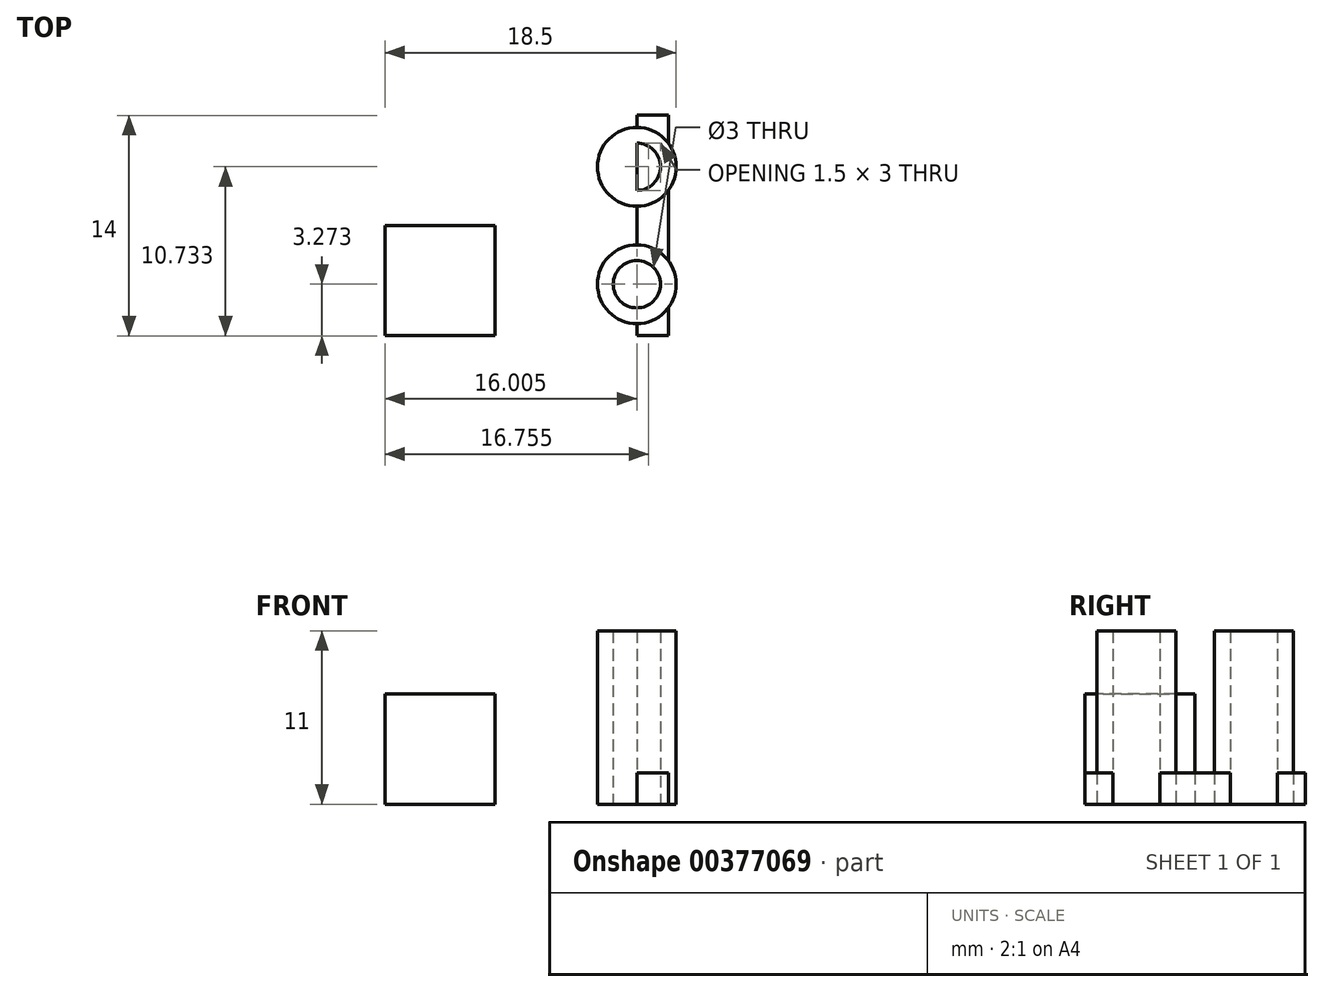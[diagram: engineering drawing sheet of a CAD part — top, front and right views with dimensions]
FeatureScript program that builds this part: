
annotation { "Feature Type Name" : "Feature", "Feature Type Description" : "" }
export const myFeature = defineFeature(function(context is Context, id is Id, definition is map)
    precondition{}
    {
        {
            var Q0;
            Q0=qCreatedBy(makeId("Top.planeOp"),FACE);
            var sketch = newSketch(context, id + "F0", { "sketchPlane" : qUnion([Q0])});
            skLineSegment(sketch, "E0.bottom", {"start": v(5.98, -1.35) * mm, "end": v(36.98, -1.35) * mm});
            skLineSegment(sketch, "E0.top", {"start": v(5.98, -15.35) * mm, "end": v(36.98, -15.35) * mm});
            skLineSegment(sketch, "E0.left", {"start": v(5.98, -1.35) * mm, "end": v(5.98, -15.35) * mm});
            skLineSegment(sketch, "E0.right", {"start": v(36.98, -1.35) * mm, "end": v(36.98, -15.35) * mm});
            skLineSegment(sketch, "E1", {"start": v(34.98, -1.35) * mm, "end": v(34.98, -15.35) * mm});
            skLineSegment(sketch, "E2", {"start": v(18.98, -15.35) * mm, "end": v(18.98, -8.35) * mm});
            skLineSegment(sketch, "E3", {"start": v(18.98, -8.35) * mm, "end": v(25.98, -8.35) * mm});
            skLineSegment(sketch, "E4", {"start": v(25.98, -8.35) * mm, "end": v(25.98, -15.35) * mm});
            skLineSegment(sketch, "E5", {"start": v(34.98, -1.35) * mm, "end": v(34.98, -3.35) * mm});
            skLineSegment(sketch, "E6", {"start": v(34.98, -3.35) * mm, "end": v(34.98, -5.89) * mm});
            skLineSegment(sketch, "E7", {"start": v(34.98, -15.35) * mm, "end": v(34.98, -13.35) * mm});
            skLineSegment(sketch, "E8", {"start": v(34.98, -13.35) * mm, "end": v(34.98, -10.8) * mm});
            skCircle(sketch, "E9", {"center": v(34.98, -12.08) * mm, "radius": 1.5 * mm});
            skCircle(sketch, "E10", {"center": v(34.98, -4.62) * mm, "radius": 1.5 * mm});
            skCircle(sketch, "E11", {"center": v(34.98, -4.62) * mm, "radius": 2.5 * mm});
            skCircle(sketch, "E12", {"center": v(34.98, -12.08) * mm, "radius": 2.5 * mm});
            skSolve(sketch);
        }
        {
            var Q0;
            {var subQ0=sQuery(id+"F0.wireOp",EDGE,"E2");Q0=makeQuery(id+"F0.imprint","IMPRINT",FACE,{"disambiguationData":[TD([[makeQuery(id+"F0.imprint","IMPRINT",EDGE,{"derivedFrom":subQ0}),-1.0]])]});}
            extrude(context, id + "F1", {"entities" : qUnion([Q0]), "depth" : 7 * mm});
        }
        {
            var Q0;
            {var subQ0=sQuery(id+"F0.wireOp",EDGE,"E10");var subQ1=sQuery(id+"F0.wireOp",EDGE,"E1");var subQ2=makeQuery(id+"F0.imprint","INTERSECT",VERTEX,{"derivedFrom":[subQ1,subQ0]});Q0=makeQuery(id+"F0.imprint","IMPRINT",FACE,{"disambiguationData":[TD([[makeQuery(id+"F0.imprint","IMPRINT",EDGE,{"disambiguationData":[TD([[subQ2,-1.0]])],"derivedFrom":subQ1}),-1.0]])]});}
            var Q1;
            {var subQ0=sQuery(id+"F0.wireOp",EDGE,"E6");Q1=makeQuery(id+"F0.imprint","IMPRINT",FACE,{"disambiguationData":[TD([[makeQuery(id+"F0.imprint","IMPRINT",EDGE,{"derivedFrom":subQ0}),-1.0]])]});}
            var Q2;
            {var subQ0=sQuery(id+"F0.wireOp",EDGE,"E6");Q2=makeQuery(id+"F0.imprint","IMPRINT",FACE,{"disambiguationData":[TD([[makeQuery(id+"F0.imprint","IMPRINT",EDGE,{"derivedFrom":subQ0}),1.0]])]});}
            var Q3;
            {var subQ5=sQuery(id+"F0.wireOp",EDGE,"E11");var subQ7=sQuery(id+"F0.wireOp",EDGE,"E0.right");var subQ8=makeQuery(id+"F0.imprint","INTERSECT",VERTEX,{"disambiguationData":[OD(0.0)],"derivedFrom":[subQ7,subQ5]});Q3=makeQuery(id+"F0.imprint","IMPRINT",FACE,{"disambiguationData":[TD([[makeQuery(id+"F0.imprint","IMPRINT",EDGE,{"disambiguationData":[TD([[subQ8,-1.0]])],"derivedFrom":subQ7}),-1.0]])]});}
            var Q4;
            {var subQ0=sQuery(id+"F0.wireOp",EDGE,"E11");var subQ1=sQuery(id+"F0.wireOp",EDGE,"E0.right");var subQ2=makeQuery(id+"F0.imprint","INTERSECT",VERTEX,{"disambiguationData":[OD(0.0)],"derivedFrom":[subQ1,subQ0]});Q4=makeQuery(id+"F0.imprint","IMPRINT",FACE,{"disambiguationData":[TD([[makeQuery(id+"F0.imprint","IMPRINT",EDGE,{"disambiguationData":[TD([[subQ2,-1.0]])],"derivedFrom":subQ1}),1.0]])]});}
            var Q5;
            {var subQ0=sQuery(id+"F0.wireOp",EDGE,"E8");Q5=makeQuery(id+"F0.imprint","IMPRINT",FACE,{"disambiguationData":[TD([[makeQuery(id+"F0.imprint","IMPRINT",EDGE,{"derivedFrom":subQ0}),-1.0]])]});}
            var Q6;
            {var subQ0=sQuery(id+"F0.wireOp",EDGE,"E12");var subQ1=sQuery(id+"F0.wireOp",EDGE,"E0.right");var subQ2=makeQuery(id+"F0.imprint","INTERSECT",VERTEX,{"disambiguationData":[OD(0.0)],"derivedFrom":[subQ1,subQ0]});Q6=makeQuery(id+"F0.imprint","IMPRINT",FACE,{"disambiguationData":[TD([[makeQuery(id+"F0.imprint","IMPRINT",EDGE,{"disambiguationData":[TD([[subQ2,-1.0]])],"derivedFrom":subQ1}),1.0]])]});}
            var Q7;
            {var subQ5=sQuery(id+"F0.wireOp",EDGE,"E12");var subQ7=sQuery(id+"F0.wireOp",EDGE,"E0.right");var subQ8=makeQuery(id+"F0.imprint","INTERSECT",VERTEX,{"disambiguationData":[OD(0.0)],"derivedFrom":[subQ7,subQ5]});Q7=makeQuery(id+"F0.imprint","IMPRINT",FACE,{"disambiguationData":[TD([[makeQuery(id+"F0.imprint","IMPRINT",EDGE,{"disambiguationData":[TD([[subQ8,-1.0]])],"derivedFrom":subQ7}),-1.0]])]});}
            var Q8;
            {var subQ0=sQuery(id+"F0.wireOp",EDGE,"E8");Q8=makeQuery(id+"F0.imprint","IMPRINT",FACE,{"disambiguationData":[TD([[makeQuery(id+"F0.imprint","IMPRINT",EDGE,{"derivedFrom":subQ0}),1.0]])]});}
            var Q9;
            {var subQ0=sQuery(id+"F0.wireOp",EDGE,"E12");var subQ1=sQuery(id+"F0.wireOp",EDGE,"E1");var subQ2=makeQuery(id+"F0.imprint","INTERSECT",VERTEX,{"derivedFrom":[subQ1,subQ0]});Q9=makeQuery(id+"F0.imprint","IMPRINT",FACE,{"disambiguationData":[TD([[makeQuery(id+"F0.imprint","IMPRINT",EDGE,{"disambiguationData":[TD([[subQ2,-1.0]])],"derivedFrom":subQ1}),-1.0]])]});}
            extrude(context, id + "F2", {"entities" : qUnion([Q0, Q1, Q2, Q3, Q4, Q5, Q6, Q7, Q8, Q9]), "depth" : 11 * mm});
        }
        {
            var Q0;
            {var subQ12=sQuery(id+"F0.wireOp",EDGE,"E0.left");Q0=makeQuery(id+"F0.imprint","IMPRINT",FACE,{"disambiguationData":[TD([[makeQuery(id+"F0.imprint","IMPRINT",EDGE,{"derivedFrom":subQ12}),1.0]])]});}
            var Q1;
            {var subQ0=sQuery(id+"F0.wireOp",EDGE,"E0.right");var subQ1=sQuery(id+"F0.wireOp",EDGE,"E0.top");var subQ2=makeQuery(id+"F0.imprint","INTERSECT",VERTEX,{"derivedFrom":[subQ1,subQ0]});Q1=makeQuery(id+"F0.imprint","IMPRINT",FACE,{"disambiguationData":[TD([[makeQuery(id+"F0.imprint","IMPRINT",EDGE,{"disambiguationData":[TD([[subQ2,1.0]])],"derivedFrom":subQ1}),1.0]])]});}
            var Q2;
            {var subQ0=sQuery(id+"F0.wireOp",EDGE,"E11");var subQ1=sQuery(id+"F0.wireOp",EDGE,"E0.right");var subQ2=makeQuery(id+"F0.imprint","INTERSECT",VERTEX,{"disambiguationData":[OD(1.0)],"derivedFrom":[subQ1,subQ0]});Q2=makeQuery(id+"F0.imprint","IMPRINT",FACE,{"disambiguationData":[TD([[makeQuery(id+"F0.imprint","IMPRINT",EDGE,{"disambiguationData":[TD([[subQ2,-1.0]])],"derivedFrom":subQ1}),-1.0]])]});}
            var Q3;
            {var subQ0=sQuery(id+"F0.wireOp",EDGE,"E0.right");var subQ1=sQuery(id+"F0.wireOp",EDGE,"E0.bottom");var subQ2=makeQuery(id+"F0.imprint","INTERSECT",VERTEX,{"derivedFrom":[subQ1,subQ0]});Q3=makeQuery(id+"F0.imprint","IMPRINT",FACE,{"disambiguationData":[TD([[makeQuery(id+"F0.imprint","IMPRINT",EDGE,{"disambiguationData":[TD([[subQ2,1.0]])],"derivedFrom":subQ1}),-1.0]])]});}
            extrude(context, id + "F3", {"entities" : qUnion([Q0, Q1, Q2, Q3]), "operationType" : NewBodyOperationType.ADD, "depth" : 2 * mm});
        }
    });
